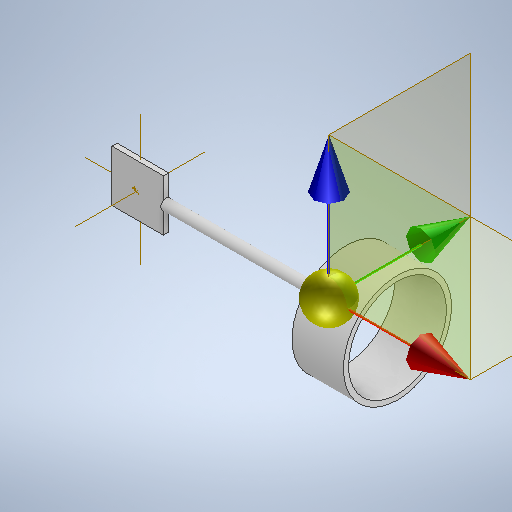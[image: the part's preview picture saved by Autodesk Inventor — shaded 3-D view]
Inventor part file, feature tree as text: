
AUTODESK INVENTOR PART (.ipt)
format: ipt  version: 2025 (Build 290162010, 162A)  size: 278,016 bytes
history: native  units: mm
features: extrude x3, sketch x3
ambient origin geometry x8: Origin, YZ Plane, XZ Plane, XY Plane, X Axis, Y Axis, Z Axis, Center Point
bodies: Solid2 (feature_tree)
feature tree (6):
  extrude  "Extrusion3"  Depth=1000.0mm
  extrude  "Extrusion4"  Depth=100.0mm
  extrude  "Extrusion6"  Depth=1000.0mm
  sketch  "Sketch3"  dims[d8=1000.0mm d9=1000.0mm]
  sketch  "Sketch4"  dims[d10=100.0mm d11=0.0mm d12=100.0mm]
  sketch  "Sketch6"  dims[d13=3500.0mm d14=0.0mm d18=1000.0mm d19=1000.0mm d20=0.0mm d21=50.0mm d22=50.0mm]
